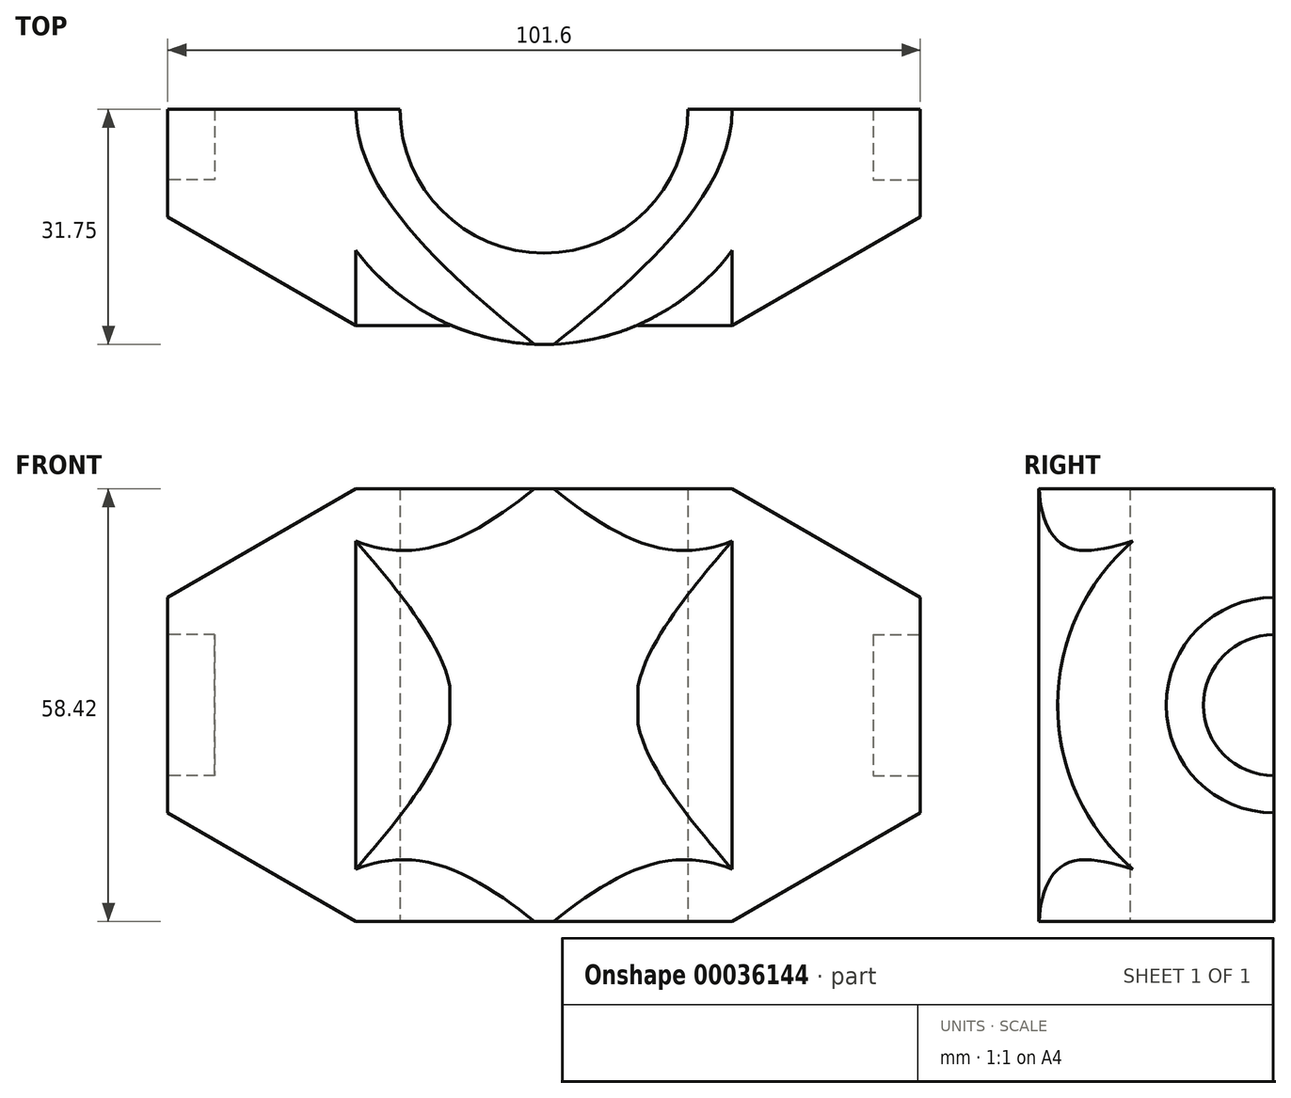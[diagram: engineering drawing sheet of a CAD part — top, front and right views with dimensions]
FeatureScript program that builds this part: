
annotation { "Feature Type Name" : "Feature", "Feature Type Description" : "" }
export const myFeature = defineFeature(function(context is Context, id is Id, definition is map)
    precondition{}
    {
        {
            var Q0;
            Q0=qCreatedBy(makeId("Top.planeOp"),FACE);
            var sketch = newSketch(context, id + "F0", { "sketchPlane" : qUnion([Q0])});
            skPoint(sketch, "E0.rect.middle", {"position": v(0, 0) * mm});
            skArc(sketch, "E1", {"start": v(-31.75, 0) * mm, "mid": v(0, -31.75) * mm, "end": v(31.75, 0) * mm});
            skLineSegment(sketch, "E2", {"start": v(-31.75, 0) * mm, "end": v(31.75, 0) * mm});
            skSolve(sketch);
        }
        {
            var Q0;
            Q0=qCreatedBy(makeId("Right.planeOp"),FACE);
            cPlane(context, id + "F1", {"entities" : qUnion([Q0]), "cplaneType" : CPlaneType.OFFSET, "offset" : 12.7 * mm, "width" : 152.4 * mm, "height" : 152.4 * mm});
        }
        {
            var Q0;
            Q0=qCreatedBy(makeId("Right.planeOp"),FACE);
            cPlane(context, id + "F2", {"entities" : qUnion([Q0]), "cplaneType" : CPlaneType.OFFSET, "offset" : 12.7 * mm, "oppositeDirection" : true, "width" : 152.4 * mm, "height" : 152.4 * mm});
        }
        {
            var Q0;
            Q0=qSketchRegion(id+"F0",true);
            extrude(context, id + "F3", {"entities" : qUnion([Q0]), "depth" : 58.42 * mm});
        }
        {
            var Q0;
            Q0=qCreatedBy(id+"F2.planeOp",FACE);
            var sketch = newSketch(context, id + "F4", { "sketchPlane" : qUnion([Q0])});
            skArc(sketch, "E3", {"start": v(0, 58.42) * mm, "mid": v(-29.21, 29.21) * mm, "end": v(0, 0) * mm});
            skLineSegment(sketch, "E4", {"start": v(0, 58.42) * mm, "end": v(0, 0) * mm});
            skSolve(sketch);
        }
        {
            var Q0;
            Q0=qSketchRegion(id+"F4",true);
            extrude(context, id + "F5", {"entities" : qUnion([Q0]), "operationType" : NewBodyOperationType.ADD, "oppositeDirection" : true, "depth" : 38.1 * mm});
        }
        {
            var Q0;
            Q0=makeQuery(id+"F5.opExtrude","CAP_FACE",FACE,{"disambiguationData":[OSD([sQuery(id+"F4.wireOp",EDGE,"E3"),sQuery(id+"F4.wireOp",EDGE,"E4")])],"isStart":false});
            var sketch = newSketch(context, id + "F6", { "sketchPlane" : qUnion([Q0])});
            skArc(sketch, "E5", {"start": v(0, 19.69) * mm, "mid": v(9.53, 29.21) * mm, "end": v(0, 38.73) * mm});
            skLineSegment(sketch, "E6", {"start": v(0, 38.73) * mm, "end": v(0, 19.69) * mm});
            skSolve(sketch);
        }
        {
            var Q0;
            Q0=qSketchRegion(id+"F6",true);
            extrude(context, id + "F7", {"entities" : qUnion([Q0]), "operationType" : NewBodyOperationType.REMOVE, "oppositeDirection" : true, "depth" : 6.35 * mm});
        }
        {
            var Q0;
            Q0=qCreatedBy(id+"F1.planeOp",FACE);
            var sketch = newSketch(context, id + "F8", { "sketchPlane" : qUnion([Q0])});
            skArc(sketch, "E7", {"start": v(0, 58.42) * mm, "mid": v(-29.2, 29.2) * mm, "end": v(0, 0) * mm});
            skPoint(sketch, "E8.rect.middle", {"position": v(0, 0) * mm});
            skLineSegment(sketch, "E9", {"start": v(0, 58.42) * mm, "end": v(0, 0) * mm});
            skSolve(sketch);
        }
        {
            var Q0;
            Q0=qSketchRegion(id+"F8",true);
            extrude(context, id + "F9", {"entities" : qUnion([Q0]), "operationType" : NewBodyOperationType.ADD, "depth" : 38.1 * mm});
        }
        {
            var Q0;
            Q0=makeQuery(id+"F9.opExtrude","CAP_FACE",FACE,{"disambiguationData":[OSD([sQuery(id+"F8.wireOp",EDGE,"E7"),sQuery(id+"F8.wireOp",EDGE,"E9")])],"isStart":false});
            var sketch = newSketch(context, id + "F10", { "sketchPlane" : qUnion([Q0])});
            skArc(sketch, "E10", {"start": v(0, 38.73) * mm, "mid": v(-9.53, 29.21) * mm, "end": v(0, 19.69) * mm});
            skLineSegment(sketch, "E11", {"start": v(0, 38.73) * mm, "end": v(0, 19.69) * mm});
            skSolve(sketch);
        }
        {
            var Q0;
            Q0=qSketchRegion(id+"F10",true);
            extrude(context, id + "F11", {"entities" : qUnion([Q0]), "operationType" : NewBodyOperationType.REMOVE, "oppositeDirection" : true, "depth" : 6.35 * mm});
        }
        {
            var Q0;
            Q0=qCreatedBy(makeId("Top.planeOp"),FACE);
            var sketch = newSketch(context, id + "F12", { "sketchPlane" : qUnion([Q0])});
            skArc(sketch, "E12", {"start": v(-19.43, 0) * mm, "mid": v(0, -19.43) * mm, "end": v(19.43, 0) * mm});
            skLineSegment(sketch, "E13", {"start": v(-19.43, 0) * mm, "end": v(19.43, 0) * mm});
            skSolve(sketch);
        }
        {
            var Q0;
            Q0=qSketchRegion(id+"F12",true);
            extrude(context, id + "F13", {"entities" : qUnion([Q0]), "operationType" : NewBodyOperationType.REMOVE, "depth" : 58.42 * mm});
        }
        {
            var Q0;
            Q0=makeQuery(id+"F5.opExtrude","CAP_EDGE",EDGE,{"disambiguationData":[OSD([sQuery(id+"F4.wireOp",EDGE,"E3")])],"isStart":false});
            chamfer(context, id + "F14", {"entities" : qUnion([Q0]), "chamferType" : ChamferType.OFFSET_ANGLE, "width" : 25.4 * mm, "oppositeDirection" : false, "angle" : 30 * degree, "tangentPropagation" : true});
        }
        {
            var Q0;
            Q0=makeQuery(id+"F9.opExtrude","CAP_EDGE",EDGE,{"disambiguationData":[OSD([sQuery(id+"F8.wireOp",EDGE,"E7")])],"isStart":false});
            chamfer(context, id + "F15", {"entities" : qUnion([Q0]), "chamferType" : ChamferType.OFFSET_ANGLE, "width" : 25.4 * mm, "oppositeDirection" : true, "angle" : 30 * degree, "tangentPropagation" : true});
        }
    });
